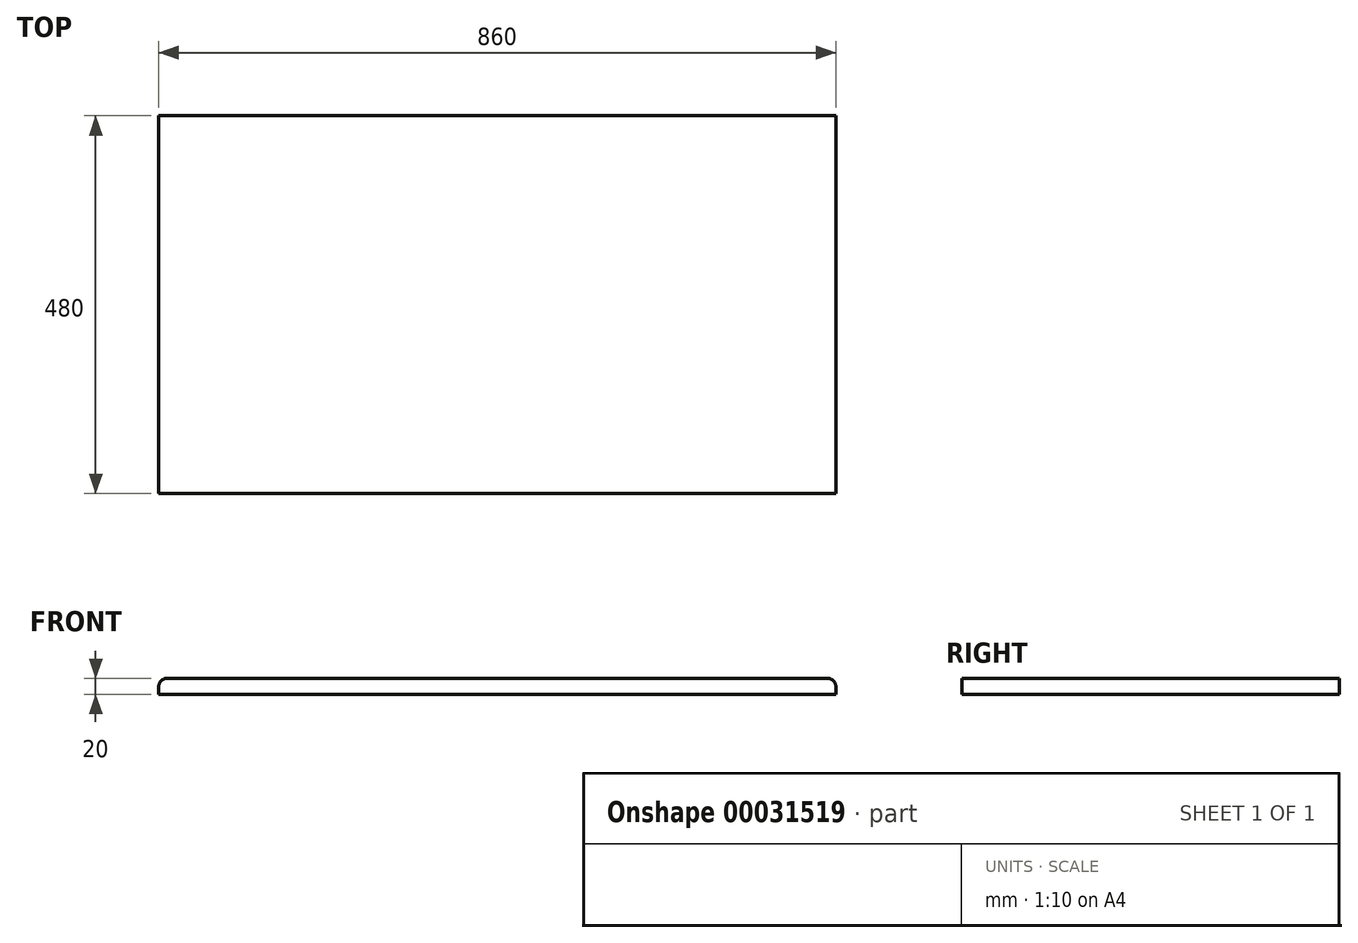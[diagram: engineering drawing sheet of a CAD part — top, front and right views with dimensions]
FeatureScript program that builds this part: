
annotation { "Feature Type Name" : "Feature", "Feature Type Description" : "" }
export const myFeature = defineFeature(function(context is Context, id is Id, definition is map)
    precondition{}
    {
        {
            var Q0;
            Q0=qCreatedBy(makeId("Front.planeOp"),FACE);
            var sketch = newSketch(context, id + "F0", { "sketchPlane" : qUnion([Q0])});
            skLineSegment(sketch, "E0.bottom", {"start": v(-238.62, 73.85) * mm, "end": v(621.38, 73.85) * mm});
            skLineSegment(sketch, "E0.top", {"start": v(-238.62, 53.85) * mm, "end": v(621.38, 53.85) * mm});
            skLineSegment(sketch, "E0.left", {"start": v(-238.62, 73.85) * mm, "end": v(-238.62, 53.85) * mm});
            skLineSegment(sketch, "E0.right", {"start": v(621.38, 73.85) * mm, "end": v(621.38, 53.85) * mm});
            skSolve(sketch);
        }
        {
            var Q0;
            Q0 = qSketchRegion(id + "F0", true);
            extrude(context, id + "F1", {"entities" : qUnion([Q0]), "oppositeDirection" : true, "depth" : 480 * mm});
        }
        {
            var Q0;
            Q0=makeQuery(id+"F1.opExtrude","SWEPT_EDGE",EDGE,{"disambiguationData":[OSD([sQuery(id+"F0.wireOp",EDGE,"E0.bottom"),sQuery(id+"F0.wireOp",EDGE,"E0.right")])]});
            var Q1;
            Q1=makeQuery(id+"F1.opExtrude","SWEPT_EDGE",EDGE,{"disambiguationData":[OSD([sQuery(id+"F0.wireOp",EDGE,"E0.bottom"),sQuery(id+"F0.wireOp",EDGE,"E0.left")])]});
            fillet(context, id + "F2", {"entities" : qUnion([Q0, Q1]), "radius" : 10 * mm, "tangentPropagation" : true, "allowEdgeOverflow" : false});
        }
    });
